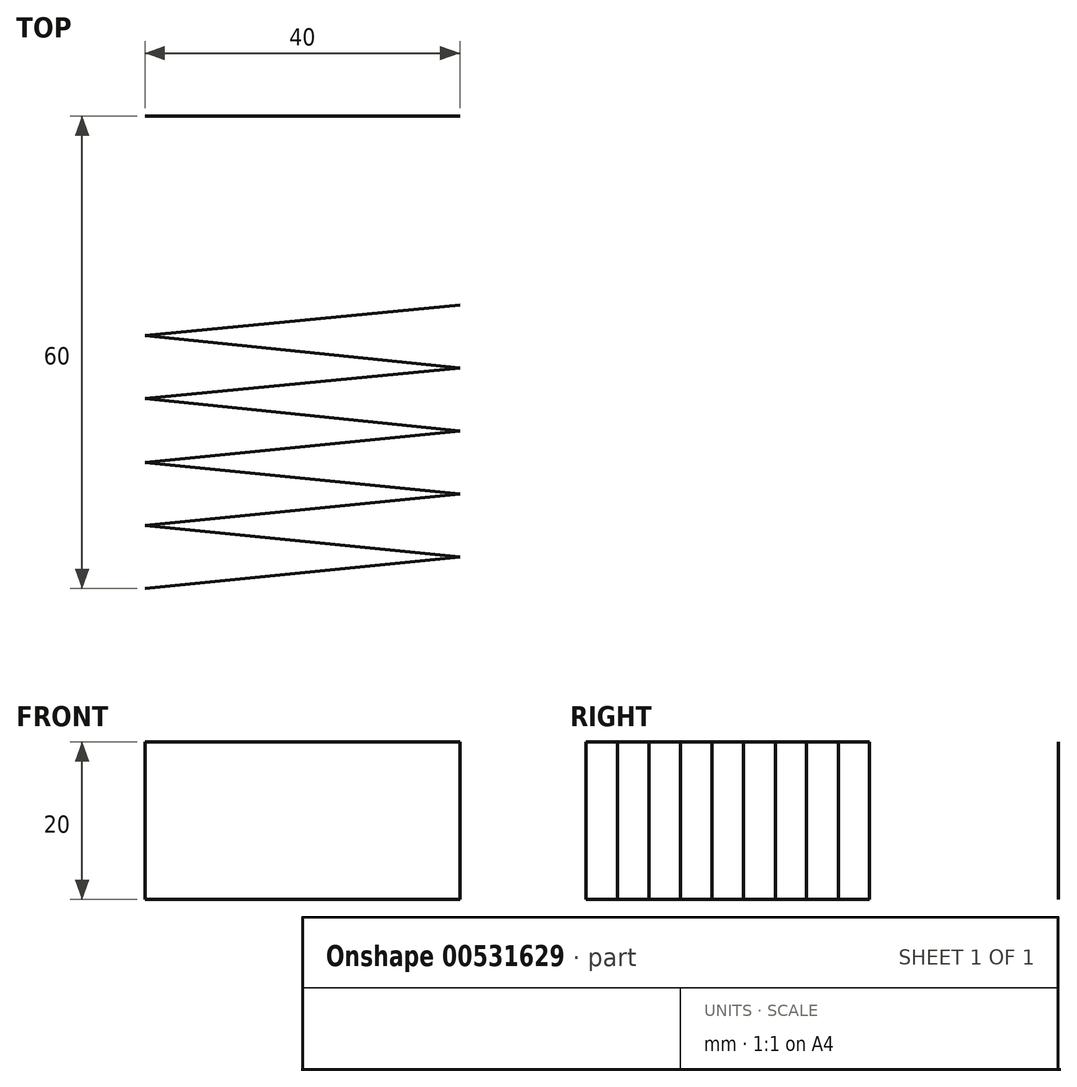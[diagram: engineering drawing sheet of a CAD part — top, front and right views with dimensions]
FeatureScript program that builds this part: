
annotation { "Feature Type Name" : "Feature", "Feature Type Description" : "" }
export const myFeature = defineFeature(function(context is Context, id is Id, definition is map)
    precondition{}
    {
        {
            var Q0;
            Q0=qCreatedBy(makeId("Top.planeOp"),FACE);
            var sketch = newSketch(context, id + "F0", { "sketchPlane" : qUnion([Q0])});
            skLineSegment(sketch, "E0.top", {"start": v(0, 35.9) * mm, "end": v(40, 35.9) * mm});
            skLineSegment(sketch, "E1", {"start": v(0, -24.1) * mm, "end": v(40, -20.1) * mm});
            skLineSegment(sketch, "E2", {"start": v(40, -20.1) * mm, "end": v(0, -16.1) * mm});
            skLineSegment(sketch, "E3", {"start": v(40, -12.1) * mm, "end": v(0, -16.1) * mm});
            skLineSegment(sketch, "E4", {"start": v(40, -4.1) * mm, "end": v(0, -8.1) * mm});
            skLineSegment(sketch, "E5", {"start": v(40, 3.9) * mm, "end": v(0, 0) * mm});
            skLineSegment(sketch, "E6", {"start": v(40, 11.9) * mm, "end": v(0, 8) * mm});
            skLineSegment(sketch, "E7", {"start": v(0, 8) * mm, "end": v(40, 3.9) * mm});
            skLineSegment(sketch, "E8", {"start": v(0, 0) * mm, "end": v(40, -4.1) * mm});
            skLineSegment(sketch, "E9", {"start": v(0, -8.1) * mm, "end": v(40, -12.1) * mm});
            skSolve(sketch);
        }
        {
            var Q0;
            Q0=qConstructionFilter(qBodyType(qCreatedBy(id+"F0",EDGE),BodyType.WIRE),ConstructionObject.NO);
            extrude(context, id + "F1", {"bodyType" : ToolBodyType.SURFACE, "surfaceEntities" : qUnion([Q0]), "depth" : 20 * mm, "offsetDistance" : 25 * mm});
        }
    });
